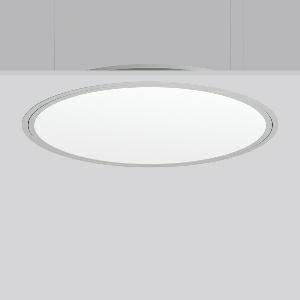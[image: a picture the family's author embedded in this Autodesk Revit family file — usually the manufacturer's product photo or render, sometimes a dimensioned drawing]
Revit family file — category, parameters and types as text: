
# Revit family: triona_round_e_312387_004_12_e797
name_source: partatom
category: Lighting Fixtures
units: mm (PartAtom-declared; Revit-internal decimal feet)

## family parameters
Cut with Voids When Loaded = No
Host = Face
Light Source = No
Part Type = Normal
Room Calculation Point = No
Round Connector Dimension = Use Diameter
Shared = No

## types (1)
- TRIONA round E (1 x LED Modul 830, 8000 lm, 3000)
    Apparent Load = 80 VA
    CIE Flux Codes = 49 80 96 100 100
    Color Rendering = 80
    Color Temperature = 3000
    Default Elevation = 1800 mm
    Description = Series: TRIONA round
Decorative round LED recessed surface luminaire. Cover made of sheet steel, powder-coated. Frame made of aluminium, powder-coated. Recessed ring: aluminium extrusion profile, powder coated. Light emission through a diffuser: plastic, opal. Lightguide and diffuser made of non-yellowing plastic (PMMA). Lateral light emission (RZB SIDELITE technology) for above-average homogeneous light distribution. Suitable for installation in cavity ceilings. Tool-free mounting system thanks to the rocker arm mechanism (patent pending). Electronic ballast included. Very easy installation thanks to Plug+Play connection. 
Colour: silver, matt (approx. RAL 9006)
Diameter: 889 mm
Height: 2 mm
Cut-out diameter: 866 mm
Recess height: 100 mm
Luminaire: recess height: 89 mm
Lamp: LED
Socket: without socket
Colour temperature: 3000K
Colour rendering index (CRI): 80
System power: 80 W
Rated luminous flux: 8000 lm
Luminous efficiency: 100 lm/W
Control gear: Converter, dimmable, DALI
Protection class: I
Type of protection: IP 40
    Height = 0 mm  [stored 0 ft]
    Lamp = 1 x LED Modul 830
    Lamp Light Flux = 8000 lm
    Lamp count = 1
    Length = 889 mm
    Lifetime = 50000 h
    Luminous efficacy = 100 lm/W
    Manufacturer = RZB
    ModVariant = No
    Model = 312387.004.12
    Mounting Place = Ceiling
    Mounting Type = Recessed
    Number of Poles = 1
    OnlyDefault = Yes
    Power Factor = 1
    Product Name = TRIONA round E
    Product group = Recessed modular luminaires
    ProductGroupID = 406
    Protection Class = Protection class I
    Protection Degree = IP 20
    RLX_Detail_Level = 1
    RLX_Emergency_Light_Flux = 0 lm
    RLX_Emergency_Type = 0
    RLX_Emergency_Type_DB = No
    RlxData = <blob elided: 39189 chars, md5=1a38e02d>
    Socket = socket
    Standby Power = 0 W
    System Light Flux = 8000 lm
    System Power = 80 W
    Type Comments = Product without accessories
    Type Image = 312387.004.12.jpg
    URL = http://relux.com
    VarID = ---
    Voltage = 230 V
    Voltage Range = 220-240 V
    Weight = 0.00 kg
    Width = 0 mm  [stored 0 ft]

note: [stored X ft] marks values corroborated as IEEE doubles in the binary element streams (Revit-internal decimal feet)

## geometry (parser evidence)
native form markers: Blend x4, Sweep x9
no freeform markers — native parametric forms only
